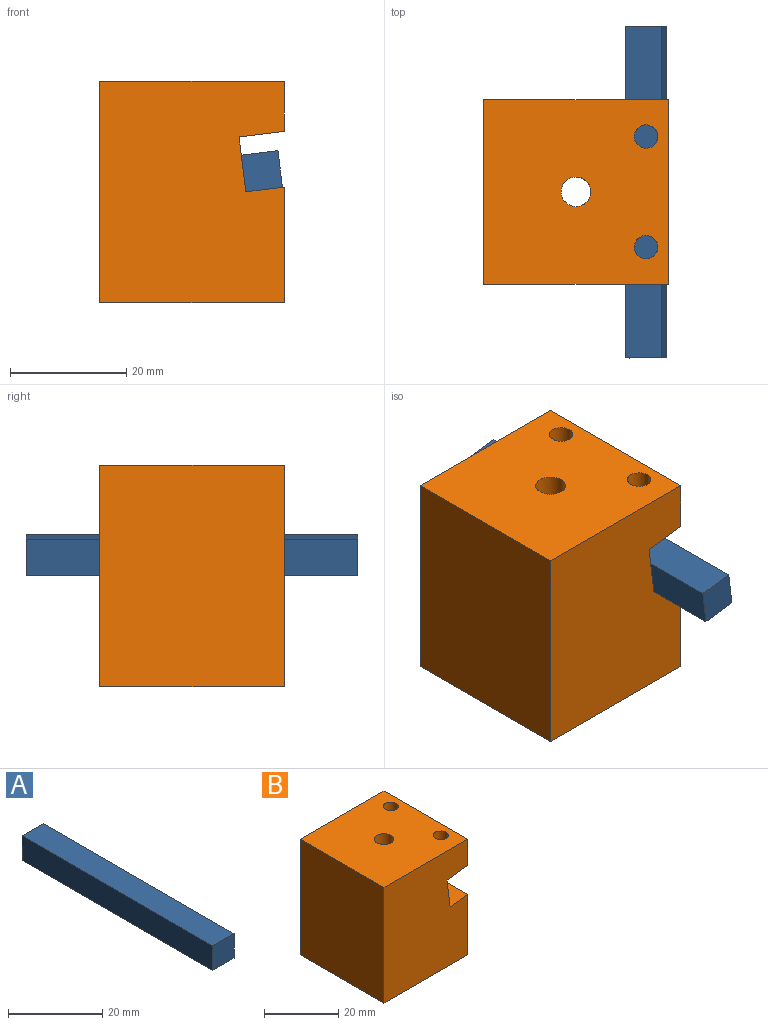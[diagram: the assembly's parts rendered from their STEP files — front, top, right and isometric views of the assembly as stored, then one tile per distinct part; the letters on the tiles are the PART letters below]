
ASSEMBLY  parts=2 mates=2
PART A: 6 faces, bbox 6.4x57.2x6.4 mm
  f0: plane 57.15x6.35mm, normal (0,0,-1), area 362.9mm2, adj f1,f3,f4,f5
  f1: plane 57.15x6.35mm, normal (1,0,0), area 362.9mm2, adj f0,f2,f4,f5
  f2: plane 57.15x6.35mm, normal (0,0,1), area 362.9mm2, adj f1,f3,f4,f5
  f3: plane 57.15x6.35mm, normal (-1,0,0), area 362.9mm2, adj f0,f2,f4,f5
  f4: plane 6.35x6.35mm, normal (0,-1,0), area 40.3mm2, adj f0,f1,f2,f3
  f5: plane 6.35x6.35mm, normal (0,1,0), area 40.3mm2, adj f0,f1,f2,f3
PART B: 15 faces, bbox 31.8x31.8x38.1 mm
  f0: plane 31.75x8.61mm, normal (1,0,0), area 273.3mm2, adj f1,f3,f5,f11
  f1: plane 38.1x31.75mm, normal (0,-1,0), area 1140.7mm2, adj f0,f2,f4,f5,f6,f10,f11,f12
  f2: plane 31.75x19.9mm, normal (1,0,0), area 631.7mm2, adj f1,f3,f6,f12
  f3: plane 38.1x31.75mm, normal (0,1,0), area 1140.7mm2, adj f0,f2,f4,f5,f6,f10,f11,f12
  f4: plane 38.1x31.75mm, normal (-1,0,0), area 1209.7mm2, adj f1,f3,f5,f6
  f5: plane 31.75x31.75mm, normal (0,0,1), area 962mm2, adj f0,f1,f3,f4,f7,f13,f14
  f6: plane 31.75x31.75mm, normal (0,0,-1), area 948.2mm2, adj f1,f2,f3,f4,f9
  f7: cylinder r=2.55mm len=12.7mm, axis (0,0,-1), area 203.7mm2, adj f5,f8
  f8: plane 8.73x8.73mm, normal (0,0,-1), area 39.4mm2, adj f7,f9
  f9: cylinder r=4.37mm len=25.4mm, axis (0,0,-1), area 696.7mm2, adj f6,f8
  f10: plane 31.75x9.45mm, normal (0.99,0,0.12), area 302.4mm2, adj f1,f3,f11,f12
  f11: plane 31.75x7.77mm, normal (0.12,0,-0.99), area 222.6mm2, adj f0,f1,f3,f10,f13,f14
  f12: plane 31.75x6.6mm, normal (-0.12,0,0.99), area 211.3mm2, adj f1,f2,f3,f10
  f13: cylinder r=2.02mm len=9.33mm, axis (0,0,1), area 115.1mm2, adj f5,f11
  f14: cylinder r=2.02mm len=9.33mm, axis (0,0,1), area 115.1mm2, adj f5,f11
PLACE A rot(axis=(0,-1,0),7deg) t=(12.04,-3.18,22.62)mm
PLACE B at identity fixed
MATE planar A.f3 <-> B.f10  axis (-0.99,0,-0.12) through (8.88,0,22.24)mm
MATE planar A.f0 <-> B.f12  axis (0.12,0,-0.99) through (12.42,0,19.47)mm
